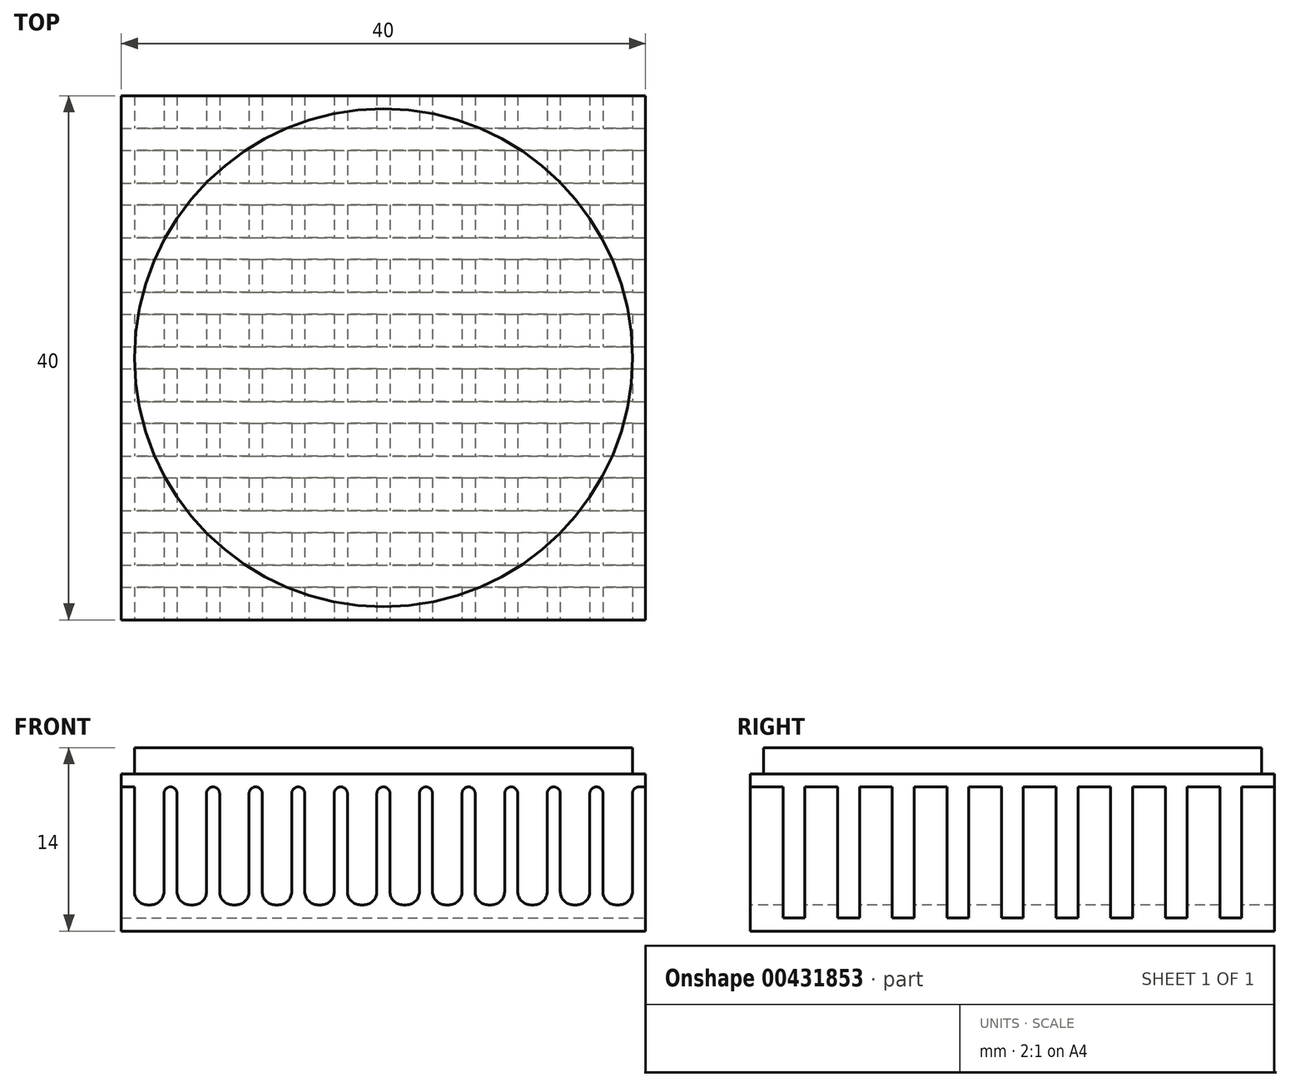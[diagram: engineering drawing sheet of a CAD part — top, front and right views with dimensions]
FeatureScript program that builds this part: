
annotation { "Feature Type Name" : "Feature", "Feature Type Description" : "" }
export const myFeature = defineFeature(function(context is Context, id is Id, definition is map)
    precondition{}
    {
        {
            var Q0;
            Q0=qCreatedBy(makeId("Top.planeOp"),FACE);
            var sketch = newSketch(context, id + "F0", { "sketchPlane" : qUnion([Q0])});
            skLineSegment(sketch, "E0.bottom", {"start": v(20, 20) * mm, "end": v(-20, 20) * mm});
            skLineSegment(sketch, "E0.top", {"start": v(20, -20) * mm, "end": v(-20, -20) * mm});
            skLineSegment(sketch, "E0.left", {"start": v(20, 20) * mm, "end": v(20, -20) * mm});
            skLineSegment(sketch, "E0.right", {"start": v(-20, 20) * mm, "end": v(-20, -20) * mm});
            skPoint(sketch, "E0.middle", {"position": v(0, 0) * mm});
            skSolve(sketch);
        }
        {
            var Q0;
            Q0=makeQuery(id+"F0.imprint","IMPRINT",FACE,{"disambiguationData":[TD([[makeQuery(id+"F0.imprint","IMPRINT",EDGE,{"derivedFrom":sQuery(id+"F0.wireOp",EDGE,"E0.bottom")}),1.0]])]});
            extrude(context, id + "F1", {"entities" : qUnion([Q0]), "depth" : 11 * mm});
        }
        {
            var Q0;
            Q0=makeQuery(id+"F1.opExtrude","SWEPT_FACE",FACE,{"disambiguationData":[OSD([sQuery(id+"F0.wireOp",EDGE,"E0.top")])]});
            var sketch = newSketch(context, id + "F2", { "sketchPlane" : qUnion([Q0])});
            skLineSegment(sketch, "E1.bottom", {"start": v(-19, 11) * mm, "end": v(-16.75, 11) * mm});
            skLineSegment(sketch, "E1.top", {"start": v(-19, 2) * mm, "end": v(-16.75, 2) * mm});
            skLineSegment(sketch, "E1.left", {"start": v(-19, 11) * mm, "end": v(-19, 2) * mm});
            skLineSegment(sketch, "E1.right", {"start": v(-16.75, 11) * mm, "end": v(-16.75, 2) * mm});
            skLineSegment(sketch, "E2.1.0.0", {"start": v(-15.75, 11) * mm, "end": v(-13.5, 11) * mm});
            skLineSegment(sketch, "E2.1.0.1", {"start": v(-13.5, 11) * mm, "end": v(-13.5, 2) * mm});
            skLineSegment(sketch, "E2.1.0.2", {"start": v(-15.75, 2) * mm, "end": v(-13.5, 2) * mm});
            skLineSegment(sketch, "E2.1.0.3", {"start": v(-15.75, 11) * mm, "end": v(-15.75, 2) * mm});
            skLineSegment(sketch, "E2.2.0.0", {"start": v(-12.5, 11) * mm, "end": v(-10.25, 11) * mm});
            skLineSegment(sketch, "E2.2.0.1", {"start": v(-10.25, 11) * mm, "end": v(-10.25, 2) * mm});
            skLineSegment(sketch, "E2.2.0.2", {"start": v(-12.5, 2) * mm, "end": v(-10.25, 2) * mm});
            skLineSegment(sketch, "E2.2.0.3", {"start": v(-12.5, 11) * mm, "end": v(-12.5, 2) * mm});
            skLineSegment(sketch, "E2.3.0.0", {"start": v(-9.25, 11) * mm, "end": v(-7, 11) * mm});
            skLineSegment(sketch, "E2.3.0.1", {"start": v(-7, 11) * mm, "end": v(-7, 2) * mm});
            skLineSegment(sketch, "E2.3.0.2", {"start": v(-9.25, 2) * mm, "end": v(-7, 2) * mm});
            skLineSegment(sketch, "E2.3.0.3", {"start": v(-9.25, 11) * mm, "end": v(-9.25, 2) * mm});
            skLineSegment(sketch, "E2.4.0.0", {"start": v(-6, 11) * mm, "end": v(-3.75, 11) * mm});
            skLineSegment(sketch, "E2.4.0.1", {"start": v(-3.75, 11) * mm, "end": v(-3.75, 2) * mm});
            skLineSegment(sketch, "E2.4.0.2", {"start": v(-6, 2) * mm, "end": v(-3.75, 2) * mm});
            skLineSegment(sketch, "E2.4.0.3", {"start": v(-6, 11) * mm, "end": v(-6, 2) * mm});
            skLineSegment(sketch, "E2.5.0.0", {"start": v(-2.75, 11) * mm, "end": v(-0.5, 11) * mm});
            skLineSegment(sketch, "E2.5.0.1", {"start": v(-0.5, 11) * mm, "end": v(-0.5, 2) * mm});
            skLineSegment(sketch, "E2.5.0.2", {"start": v(-2.75, 2) * mm, "end": v(-0.5, 2) * mm});
            skLineSegment(sketch, "E2.5.0.3", {"start": v(-2.75, 11) * mm, "end": v(-2.75, 2) * mm});
            skLineSegment(sketch, "E2.6.0.0", {"start": v(0.5, 11) * mm, "end": v(2.75, 11) * mm});
            skLineSegment(sketch, "E2.6.0.1", {"start": v(2.75, 11) * mm, "end": v(2.75, 2) * mm});
            skLineSegment(sketch, "E2.6.0.2", {"start": v(0.5, 2) * mm, "end": v(2.75, 2) * mm});
            skLineSegment(sketch, "E2.6.0.3", {"start": v(0.5, 11) * mm, "end": v(0.5, 2) * mm});
            skLineSegment(sketch, "E2.7.0.0", {"start": v(3.75, 11) * mm, "end": v(6, 11) * mm});
            skLineSegment(sketch, "E2.7.0.1", {"start": v(6, 11) * mm, "end": v(6, 2) * mm});
            skLineSegment(sketch, "E2.7.0.2", {"start": v(3.75, 2) * mm, "end": v(6, 2) * mm});
            skLineSegment(sketch, "E2.7.0.3", {"start": v(3.75, 11) * mm, "end": v(3.75, 2) * mm});
            skLineSegment(sketch, "E2.8.0.0", {"start": v(7, 11) * mm, "end": v(9.25, 11) * mm});
            skLineSegment(sketch, "E2.8.0.1", {"start": v(9.25, 11) * mm, "end": v(9.25, 2) * mm});
            skLineSegment(sketch, "E2.8.0.2", {"start": v(7, 2) * mm, "end": v(9.25, 2) * mm});
            skLineSegment(sketch, "E2.8.0.3", {"start": v(7, 11) * mm, "end": v(7, 2) * mm});
            skLineSegment(sketch, "E2.9.0.0", {"start": v(10.25, 11) * mm, "end": v(12.5, 11) * mm});
            skLineSegment(sketch, "E2.9.0.1", {"start": v(12.5, 11) * mm, "end": v(12.5, 2) * mm});
            skLineSegment(sketch, "E2.9.0.2", {"start": v(10.25, 2) * mm, "end": v(12.5, 2) * mm});
            skLineSegment(sketch, "E2.9.0.3", {"start": v(10.25, 11) * mm, "end": v(10.25, 2) * mm});
            skLineSegment(sketch, "E2.10.0.0", {"start": v(13.5, 11) * mm, "end": v(15.75, 11) * mm});
            skLineSegment(sketch, "E2.10.0.1", {"start": v(15.75, 11) * mm, "end": v(15.75, 2) * mm});
            skLineSegment(sketch, "E2.10.0.2", {"start": v(13.5, 2) * mm, "end": v(15.75, 2) * mm});
            skLineSegment(sketch, "E2.10.0.3", {"start": v(13.5, 11) * mm, "end": v(13.5, 2) * mm});
            skLineSegment(sketch, "E2.11.0.0", {"start": v(16.75, 11) * mm, "end": v(19, 11) * mm});
            skLineSegment(sketch, "E2.11.0.1", {"start": v(19, 11) * mm, "end": v(19, 2) * mm});
            skLineSegment(sketch, "E2.11.0.2", {"start": v(16.75, 2) * mm, "end": v(19, 2) * mm});
            skLineSegment(sketch, "E2.11.0.3", {"start": v(16.75, 11) * mm, "end": v(16.75, 2) * mm});
            skLineSegment(sketch, "E2.direction1", {"start": v(-19, 11) * mm, "end": v(-15.75, 11) * mm, "construction": true});
            skSolve(sketch);
        }
        {
            var Q0;
            Q0 = qSketchRegion(id + "F2", true);
            extrude(context, id + "F3", {"entities" : qUnion([Q0]), "operationType" : NewBodyOperationType.REMOVE, "oppositeDirection" : true, "depth" : 40 * mm});
        }
        {
            var Q0;
            Q0=makeQuery(id+"F3.boolean.opBoolean","COPY",EDGE,{"derivedFrom":makeQuery(id+"F3.opExtrude","SWEPT_EDGE",EDGE,{"disambiguationData":[OSD([sQuery(id+"F0.wireOp",EDGE,"E0.top"),sQuery(id+"F2.wireOp",EDGE,"E2.11.0.0"),sQuery(id+"F2.wireOp",EDGE,"E2.11.0.1")])]})});
            var Q1;
            Q1=makeQuery(id+"F3.boolean.opBoolean","COPY",EDGE,{"derivedFrom":makeQuery(id+"F3.opExtrude","SWEPT_EDGE",EDGE,{"disambiguationData":[OSD([sQuery(id+"F0.wireOp",EDGE,"E0.top"),sQuery(id+"F2.wireOp",EDGE,"E2.11.0.0"),sQuery(id+"F2.wireOp",EDGE,"E2.11.0.3")])]})});
            var Q2;
            Q2=makeQuery(id+"F3.boolean.opBoolean","COPY",EDGE,{"derivedFrom":makeQuery(id+"F3.opExtrude","SWEPT_EDGE",EDGE,{"disambiguationData":[OSD([sQuery(id+"F0.wireOp",EDGE,"E0.top"),sQuery(id+"F2.wireOp",EDGE,"E2.10.0.0"),sQuery(id+"F2.wireOp",EDGE,"E2.10.0.1")])]})});
            var Q3;
            Q3=makeQuery(id+"F3.boolean.opBoolean","COPY",EDGE,{"derivedFrom":makeQuery(id+"F3.opExtrude","SWEPT_EDGE",EDGE,{"disambiguationData":[OSD([sQuery(id+"F0.wireOp",EDGE,"E0.top"),sQuery(id+"F2.wireOp",EDGE,"E2.10.0.0"),sQuery(id+"F2.wireOp",EDGE,"E2.10.0.3")])]})});
            var Q4;
            Q4=makeQuery(id+"F3.boolean.opBoolean","COPY",EDGE,{"derivedFrom":makeQuery(id+"F3.opExtrude","SWEPT_EDGE",EDGE,{"disambiguationData":[OSD([sQuery(id+"F0.wireOp",EDGE,"E0.top"),sQuery(id+"F2.wireOp",EDGE,"E2.9.0.0"),sQuery(id+"F2.wireOp",EDGE,"E2.9.0.1")])]})});
            var Q5;
            Q5=makeQuery(id+"F3.boolean.opBoolean","COPY",EDGE,{"derivedFrom":makeQuery(id+"F3.opExtrude","SWEPT_EDGE",EDGE,{"disambiguationData":[OSD([sQuery(id+"F0.wireOp",EDGE,"E0.top"),sQuery(id+"F2.wireOp",EDGE,"E2.9.0.0"),sQuery(id+"F2.wireOp",EDGE,"E2.9.0.3")])]})});
            var Q6;
            Q6=makeQuery(id+"F3.boolean.opBoolean","COPY",EDGE,{"derivedFrom":makeQuery(id+"F3.opExtrude","SWEPT_EDGE",EDGE,{"disambiguationData":[OSD([sQuery(id+"F0.wireOp",EDGE,"E0.top"),sQuery(id+"F2.wireOp",EDGE,"E2.8.0.0"),sQuery(id+"F2.wireOp",EDGE,"E2.8.0.1")])]})});
            var Q7;
            Q7=makeQuery(id+"F3.boolean.opBoolean","COPY",EDGE,{"derivedFrom":makeQuery(id+"F3.opExtrude","SWEPT_EDGE",EDGE,{"disambiguationData":[OSD([sQuery(id+"F0.wireOp",EDGE,"E0.top"),sQuery(id+"F2.wireOp",EDGE,"E2.8.0.0"),sQuery(id+"F2.wireOp",EDGE,"E2.8.0.3")])]})});
            var Q8;
            Q8=makeQuery(id+"F3.boolean.opBoolean","COPY",EDGE,{"derivedFrom":makeQuery(id+"F3.opExtrude","SWEPT_EDGE",EDGE,{"disambiguationData":[OSD([sQuery(id+"F0.wireOp",EDGE,"E0.top"),sQuery(id+"F2.wireOp",EDGE,"E2.7.0.0"),sQuery(id+"F2.wireOp",EDGE,"E2.7.0.1")])]})});
            var Q9;
            Q9=makeQuery(id+"F3.boolean.opBoolean","COPY",EDGE,{"derivedFrom":makeQuery(id+"F3.opExtrude","SWEPT_EDGE",EDGE,{"disambiguationData":[OSD([sQuery(id+"F0.wireOp",EDGE,"E0.top"),sQuery(id+"F2.wireOp",EDGE,"E2.7.0.0"),sQuery(id+"F2.wireOp",EDGE,"E2.7.0.3")])]})});
            var Q10;
            Q10=makeQuery(id+"F3.boolean.opBoolean","COPY",EDGE,{"derivedFrom":makeQuery(id+"F3.opExtrude","SWEPT_EDGE",EDGE,{"disambiguationData":[OSD([sQuery(id+"F0.wireOp",EDGE,"E0.top"),sQuery(id+"F2.wireOp",EDGE,"E2.6.0.0"),sQuery(id+"F2.wireOp",EDGE,"E2.6.0.3")])]})});
            var Q11;
            Q11=makeQuery(id+"F3.boolean.opBoolean","COPY",EDGE,{"derivedFrom":makeQuery(id+"F3.opExtrude","SWEPT_EDGE",EDGE,{"disambiguationData":[OSD([sQuery(id+"F0.wireOp",EDGE,"E0.top"),sQuery(id+"F2.wireOp",EDGE,"E2.5.0.0"),sQuery(id+"F2.wireOp",EDGE,"E2.5.0.1")])]})});
            var Q12;
            Q12=makeQuery(id+"F3.boolean.opBoolean","COPY",EDGE,{"derivedFrom":makeQuery(id+"F3.opExtrude","SWEPT_EDGE",EDGE,{"disambiguationData":[OSD([sQuery(id+"F0.wireOp",EDGE,"E0.top"),sQuery(id+"F2.wireOp",EDGE,"E2.5.0.0"),sQuery(id+"F2.wireOp",EDGE,"E2.5.0.3")])]})});
            var Q13;
            Q13=makeQuery(id+"F3.boolean.opBoolean","COPY",EDGE,{"derivedFrom":makeQuery(id+"F3.opExtrude","SWEPT_EDGE",EDGE,{"disambiguationData":[OSD([sQuery(id+"F0.wireOp",EDGE,"E0.top"),sQuery(id+"F2.wireOp",EDGE,"E2.4.0.0"),sQuery(id+"F2.wireOp",EDGE,"E2.4.0.1")])]})});
            var Q14;
            Q14=makeQuery(id+"F3.boolean.opBoolean","COPY",EDGE,{"derivedFrom":makeQuery(id+"F3.opExtrude","SWEPT_EDGE",EDGE,{"disambiguationData":[OSD([sQuery(id+"F0.wireOp",EDGE,"E0.top"),sQuery(id+"F2.wireOp",EDGE,"E2.4.0.0"),sQuery(id+"F2.wireOp",EDGE,"E2.4.0.3")])]})});
            var Q15;
            Q15=makeQuery(id+"F3.boolean.opBoolean","COPY",EDGE,{"derivedFrom":makeQuery(id+"F3.opExtrude","SWEPT_EDGE",EDGE,{"disambiguationData":[OSD([sQuery(id+"F0.wireOp",EDGE,"E0.top"),sQuery(id+"F2.wireOp",EDGE,"E2.3.0.0"),sQuery(id+"F2.wireOp",EDGE,"E2.3.0.1")])]})});
            var Q16;
            Q16=makeQuery(id+"F3.boolean.opBoolean","COPY",EDGE,{"derivedFrom":makeQuery(id+"F3.opExtrude","SWEPT_EDGE",EDGE,{"disambiguationData":[OSD([sQuery(id+"F0.wireOp",EDGE,"E0.top"),sQuery(id+"F2.wireOp",EDGE,"E2.3.0.0"),sQuery(id+"F2.wireOp",EDGE,"E2.3.0.3")])]})});
            var Q17;
            Q17=makeQuery(id+"F3.boolean.opBoolean","COPY",EDGE,{"derivedFrom":makeQuery(id+"F3.opExtrude","SWEPT_EDGE",EDGE,{"disambiguationData":[OSD([sQuery(id+"F0.wireOp",EDGE,"E0.top"),sQuery(id+"F2.wireOp",EDGE,"E2.2.0.0"),sQuery(id+"F2.wireOp",EDGE,"E2.2.0.1")])]})});
            var Q18;
            Q18=makeQuery(id+"F3.boolean.opBoolean","COPY",EDGE,{"derivedFrom":makeQuery(id+"F3.opExtrude","SWEPT_EDGE",EDGE,{"disambiguationData":[OSD([sQuery(id+"F0.wireOp",EDGE,"E0.top"),sQuery(id+"F2.wireOp",EDGE,"E2.2.0.0"),sQuery(id+"F2.wireOp",EDGE,"E2.2.0.3")])]})});
            var Q19;
            Q19=makeQuery(id+"F3.boolean.opBoolean","COPY",EDGE,{"derivedFrom":makeQuery(id+"F3.opExtrude","SWEPT_EDGE",EDGE,{"disambiguationData":[OSD([sQuery(id+"F0.wireOp",EDGE,"E0.top"),sQuery(id+"F2.wireOp",EDGE,"E2.1.0.0"),sQuery(id+"F2.wireOp",EDGE,"E2.1.0.1")])]})});
            var Q20;
            Q20=makeQuery(id+"F3.boolean.opBoolean","COPY",EDGE,{"derivedFrom":makeQuery(id+"F3.opExtrude","SWEPT_EDGE",EDGE,{"disambiguationData":[OSD([sQuery(id+"F0.wireOp",EDGE,"E0.top"),sQuery(id+"F2.wireOp",EDGE,"E2.1.0.0"),sQuery(id+"F2.wireOp",EDGE,"E2.1.0.3")])]})});
            var Q21;
            Q21=makeQuery(id+"F3.boolean.opBoolean","COPY",EDGE,{"derivedFrom":makeQuery(id+"F3.opExtrude","SWEPT_EDGE",EDGE,{"disambiguationData":[OSD([sQuery(id+"F0.wireOp",EDGE,"E0.top"),sQuery(id+"F2.wireOp",EDGE,"E1.bottom"),sQuery(id+"F2.wireOp",EDGE,"E1.right")])]})});
            var Q22;
            Q22=makeQuery(id+"F3.boolean.opBoolean","COPY",EDGE,{"derivedFrom":makeQuery(id+"F3.opExtrude","SWEPT_EDGE",EDGE,{"disambiguationData":[OSD([sQuery(id+"F0.wireOp",EDGE,"E0.top"),sQuery(id+"F2.wireOp",EDGE,"E1.bottom"),sQuery(id+"F2.wireOp",EDGE,"E1.left")])]})});
            var Q23;
            Q23=makeQuery(id+"F3.boolean.opBoolean","COPY",EDGE,{"derivedFrom":makeQuery(id+"F3.opExtrude","SWEPT_EDGE",EDGE,{"disambiguationData":[OSD([sQuery(id+"F0.wireOp",EDGE,"E0.top"),sQuery(id+"F2.wireOp",EDGE,"E2.6.0.0"),sQuery(id+"F2.wireOp",EDGE,"E2.6.0.1")])]})});
            fillet(context, id + "F4", {"entities" : qUnion([Q0, Q1, Q2, Q3, Q4, Q5, Q6, Q7, Q8, Q9, Q10, Q11, Q12, Q13, Q14, Q15, Q16, Q17, Q18, Q19, Q20, Q21, Q22, Q23]), "radius" : 0.5 * mm, "tangentPropagation" : true, "allowEdgeOverflow" : false});
        }
        {
            var Q0;
            Q0=makeQuery(id+"F3.boolean.opBoolean","COPY",EDGE,{"derivedFrom":makeQuery(id+"F3.opExtrude","SWEPT_EDGE",EDGE,{"disambiguationData":[OSD([sQuery(id+"F2.wireOp",EDGE,"E1.top"),sQuery(id+"F2.wireOp",EDGE,"E1.left")])]})});
            var Q1;
            Q1=makeQuery(id+"F3.boolean.opBoolean","COPY",EDGE,{"derivedFrom":makeQuery(id+"F3.opExtrude","SWEPT_EDGE",EDGE,{"disambiguationData":[OSD([sQuery(id+"F2.wireOp",EDGE,"E2.1.0.2"),sQuery(id+"F2.wireOp",EDGE,"E2.1.0.3")])]})});
            var Q2;
            Q2=makeQuery(id+"F3.boolean.opBoolean","COPY",EDGE,{"derivedFrom":makeQuery(id+"F3.opExtrude","SWEPT_EDGE",EDGE,{"disambiguationData":[OSD([sQuery(id+"F2.wireOp",EDGE,"E2.2.0.2"),sQuery(id+"F2.wireOp",EDGE,"E2.2.0.3")])]})});
            var Q3;
            Q3=makeQuery(id+"F3.boolean.opBoolean","COPY",EDGE,{"derivedFrom":makeQuery(id+"F3.opExtrude","SWEPT_EDGE",EDGE,{"disambiguationData":[OSD([sQuery(id+"F2.wireOp",EDGE,"E2.3.0.2"),sQuery(id+"F2.wireOp",EDGE,"E2.3.0.3")])]})});
            var Q4;
            Q4=makeQuery(id+"F3.boolean.opBoolean","COPY",EDGE,{"derivedFrom":makeQuery(id+"F3.opExtrude","SWEPT_EDGE",EDGE,{"disambiguationData":[OSD([sQuery(id+"F2.wireOp",EDGE,"E2.4.0.2"),sQuery(id+"F2.wireOp",EDGE,"E2.4.0.3")])]})});
            var Q5;
            Q5=makeQuery(id+"F3.boolean.opBoolean","COPY",EDGE,{"derivedFrom":makeQuery(id+"F3.opExtrude","SWEPT_EDGE",EDGE,{"disambiguationData":[OSD([sQuery(id+"F2.wireOp",EDGE,"E2.5.0.2"),sQuery(id+"F2.wireOp",EDGE,"E2.5.0.3")])]})});
            var Q6;
            Q6=makeQuery(id+"F3.boolean.opBoolean","COPY",EDGE,{"derivedFrom":makeQuery(id+"F3.opExtrude","SWEPT_EDGE",EDGE,{"disambiguationData":[OSD([sQuery(id+"F2.wireOp",EDGE,"E2.6.0.2"),sQuery(id+"F2.wireOp",EDGE,"E2.6.0.3")])]})});
            var Q7;
            Q7=makeQuery(id+"F3.boolean.opBoolean","COPY",EDGE,{"derivedFrom":makeQuery(id+"F3.opExtrude","SWEPT_EDGE",EDGE,{"disambiguationData":[OSD([sQuery(id+"F2.wireOp",EDGE,"E2.7.0.2"),sQuery(id+"F2.wireOp",EDGE,"E2.7.0.3")])]})});
            var Q8;
            Q8=makeQuery(id+"F3.boolean.opBoolean","COPY",EDGE,{"derivedFrom":makeQuery(id+"F3.opExtrude","SWEPT_EDGE",EDGE,{"disambiguationData":[OSD([sQuery(id+"F2.wireOp",EDGE,"E2.8.0.2"),sQuery(id+"F2.wireOp",EDGE,"E2.8.0.3")])]})});
            var Q9;
            Q9=makeQuery(id+"F3.boolean.opBoolean","COPY",EDGE,{"derivedFrom":makeQuery(id+"F3.opExtrude","SWEPT_EDGE",EDGE,{"disambiguationData":[OSD([sQuery(id+"F2.wireOp",EDGE,"E2.9.0.2"),sQuery(id+"F2.wireOp",EDGE,"E2.9.0.3")])]})});
            var Q10;
            Q10=makeQuery(id+"F3.boolean.opBoolean","COPY",EDGE,{"derivedFrom":makeQuery(id+"F3.opExtrude","SWEPT_EDGE",EDGE,{"disambiguationData":[OSD([sQuery(id+"F2.wireOp",EDGE,"E2.10.0.2"),sQuery(id+"F2.wireOp",EDGE,"E2.10.0.3")])]})});
            var Q11;
            Q11=makeQuery(id+"F3.boolean.opBoolean","COPY",EDGE,{"derivedFrom":makeQuery(id+"F3.opExtrude","SWEPT_EDGE",EDGE,{"disambiguationData":[OSD([sQuery(id+"F2.wireOp",EDGE,"E2.11.0.2"),sQuery(id+"F2.wireOp",EDGE,"E2.11.0.3")])]})});
            var Q12;
            Q12=makeQuery(id+"F3.boolean.opBoolean","COPY",EDGE,{"derivedFrom":makeQuery(id+"F3.opExtrude","SWEPT_EDGE",EDGE,{"disambiguationData":[OSD([sQuery(id+"F2.wireOp",EDGE,"E1.top"),sQuery(id+"F2.wireOp",EDGE,"E1.right")])]})});
            var Q13;
            Q13=makeQuery(id+"F3.boolean.opBoolean","COPY",EDGE,{"derivedFrom":makeQuery(id+"F3.opExtrude","SWEPT_EDGE",EDGE,{"disambiguationData":[OSD([sQuery(id+"F2.wireOp",EDGE,"E2.1.0.1"),sQuery(id+"F2.wireOp",EDGE,"E2.1.0.2")])]})});
            var Q14;
            Q14=makeQuery(id+"F3.boolean.opBoolean","COPY",EDGE,{"derivedFrom":makeQuery(id+"F3.opExtrude","SWEPT_EDGE",EDGE,{"disambiguationData":[OSD([sQuery(id+"F2.wireOp",EDGE,"E2.2.0.1"),sQuery(id+"F2.wireOp",EDGE,"E2.2.0.2")])]})});
            var Q15;
            Q15=makeQuery(id+"F3.boolean.opBoolean","COPY",EDGE,{"derivedFrom":makeQuery(id+"F3.opExtrude","SWEPT_EDGE",EDGE,{"disambiguationData":[OSD([sQuery(id+"F2.wireOp",EDGE,"E2.3.0.1"),sQuery(id+"F2.wireOp",EDGE,"E2.3.0.2")])]})});
            var Q16;
            Q16=makeQuery(id+"F3.boolean.opBoolean","COPY",EDGE,{"derivedFrom":makeQuery(id+"F3.opExtrude","SWEPT_EDGE",EDGE,{"disambiguationData":[OSD([sQuery(id+"F2.wireOp",EDGE,"E2.4.0.1"),sQuery(id+"F2.wireOp",EDGE,"E2.4.0.2")])]})});
            var Q17;
            Q17=makeQuery(id+"F3.boolean.opBoolean","COPY",EDGE,{"derivedFrom":makeQuery(id+"F3.opExtrude","SWEPT_EDGE",EDGE,{"disambiguationData":[OSD([sQuery(id+"F2.wireOp",EDGE,"E2.5.0.1"),sQuery(id+"F2.wireOp",EDGE,"E2.5.0.2")])]})});
            var Q18;
            Q18=makeQuery(id+"F3.boolean.opBoolean","COPY",EDGE,{"derivedFrom":makeQuery(id+"F3.opExtrude","SWEPT_EDGE",EDGE,{"disambiguationData":[OSD([sQuery(id+"F2.wireOp",EDGE,"E2.6.0.1"),sQuery(id+"F2.wireOp",EDGE,"E2.6.0.2")])]})});
            var Q19;
            Q19=makeQuery(id+"F3.boolean.opBoolean","COPY",EDGE,{"derivedFrom":makeQuery(id+"F3.opExtrude","SWEPT_EDGE",EDGE,{"disambiguationData":[OSD([sQuery(id+"F2.wireOp",EDGE,"E2.7.0.1"),sQuery(id+"F2.wireOp",EDGE,"E2.7.0.2")])]})});
            var Q20;
            Q20=makeQuery(id+"F3.boolean.opBoolean","COPY",EDGE,{"derivedFrom":makeQuery(id+"F3.opExtrude","SWEPT_EDGE",EDGE,{"disambiguationData":[OSD([sQuery(id+"F2.wireOp",EDGE,"E2.8.0.1"),sQuery(id+"F2.wireOp",EDGE,"E2.8.0.2")])]})});
            var Q21;
            Q21=makeQuery(id+"F3.boolean.opBoolean","COPY",EDGE,{"derivedFrom":makeQuery(id+"F3.opExtrude","SWEPT_EDGE",EDGE,{"disambiguationData":[OSD([sQuery(id+"F2.wireOp",EDGE,"E2.9.0.1"),sQuery(id+"F2.wireOp",EDGE,"E2.9.0.2")])]})});
            var Q22;
            Q22=makeQuery(id+"F3.boolean.opBoolean","COPY",EDGE,{"derivedFrom":makeQuery(id+"F3.opExtrude","SWEPT_EDGE",EDGE,{"disambiguationData":[OSD([sQuery(id+"F2.wireOp",EDGE,"E2.10.0.1"),sQuery(id+"F2.wireOp",EDGE,"E2.10.0.2")])]})});
            var Q23;
            Q23=makeQuery(id+"F3.boolean.opBoolean","COPY",EDGE,{"derivedFrom":makeQuery(id+"F3.opExtrude","SWEPT_EDGE",EDGE,{"disambiguationData":[OSD([sQuery(id+"F2.wireOp",EDGE,"E2.11.0.1"),sQuery(id+"F2.wireOp",EDGE,"E2.11.0.2")])]})});
            fillet(context, id + "F5", {"entities" : qUnion([Q0, Q1, Q2, Q3, Q4, Q5, Q6, Q7, Q8, Q9, Q10, Q11, Q12, Q13, Q14, Q15, Q16, Q17, Q18, Q19, Q20, Q21, Q22, Q23]), "radius" : 1 * mm, "tangentPropagation" : true, "allowEdgeOverflow" : false});
        }
        {
            var Q0;
            Q0=makeQuery(id+"F1.opExtrude","SWEPT_FACE",FACE,{"disambiguationData":[OSD([sQuery(id+"F0.wireOp",EDGE,"E0.left")])]});
            var sketch = newSketch(context, id + "F6", { "sketchPlane" : qUnion([Q0])});
            skLineSegment(sketch, "E3.bottom", {"start": v(-17.5, 1) * mm, "end": v(-15.83, 1) * mm});
            skLineSegment(sketch, "E3.top", {"start": v(-17.5, 11) * mm, "end": v(-15.83, 11) * mm});
            skLineSegment(sketch, "E3.left", {"start": v(-17.5, 1) * mm, "end": v(-17.5, 11) * mm});
            skLineSegment(sketch, "E3.right", {"start": v(-15.83, 1) * mm, "end": v(-15.83, 11) * mm});
            skLineSegment(sketch, "E4.1.0.0", {"start": v(-11.67, 1) * mm, "end": v(-11.67, 11) * mm});
            skLineSegment(sketch, "E4.1.0.1", {"start": v(-13.33, 11) * mm, "end": v(-11.67, 11) * mm});
            skLineSegment(sketch, "E4.1.0.2", {"start": v(-13.33, 1) * mm, "end": v(-13.33, 11) * mm});
            skLineSegment(sketch, "E4.1.0.3", {"start": v(-13.33, 1) * mm, "end": v(-11.67, 1) * mm});
            skLineSegment(sketch, "E4.2.0.0", {"start": v(-7.5, 1) * mm, "end": v(-7.5, 11) * mm});
            skLineSegment(sketch, "E4.2.0.1", {"start": v(-9.17, 11) * mm, "end": v(-7.5, 11) * mm});
            skLineSegment(sketch, "E4.2.0.2", {"start": v(-9.17, 1) * mm, "end": v(-9.17, 11) * mm});
            skLineSegment(sketch, "E4.2.0.3", {"start": v(-9.17, 1) * mm, "end": v(-7.5, 1) * mm});
            skLineSegment(sketch, "E4.3.0.0", {"start": v(-3.33, 1) * mm, "end": v(-3.33, 11) * mm});
            skLineSegment(sketch, "E4.3.0.1", {"start": v(-5, 11) * mm, "end": v(-3.33, 11) * mm});
            skLineSegment(sketch, "E4.3.0.2", {"start": v(-5, 1) * mm, "end": v(-5, 11) * mm});
            skLineSegment(sketch, "E4.3.0.3", {"start": v(-5, 1) * mm, "end": v(-3.33, 1) * mm});
            skLineSegment(sketch, "E4.4.0.0", {"start": v(0.83, 1) * mm, "end": v(0.83, 11) * mm});
            skLineSegment(sketch, "E4.4.0.1", {"start": v(-0.83, 11) * mm, "end": v(0.83, 11) * mm});
            skLineSegment(sketch, "E4.4.0.2", {"start": v(-0.83, 1) * mm, "end": v(-0.83, 11) * mm});
            skLineSegment(sketch, "E4.4.0.3", {"start": v(-0.83, 1) * mm, "end": v(0.83, 1) * mm});
            skLineSegment(sketch, "E4.5.0.0", {"start": v(5, 1) * mm, "end": v(5, 11) * mm});
            skLineSegment(sketch, "E4.5.0.1", {"start": v(3.33, 11) * mm, "end": v(5, 11) * mm});
            skLineSegment(sketch, "E4.5.0.2", {"start": v(3.33, 1) * mm, "end": v(3.33, 11) * mm});
            skLineSegment(sketch, "E4.5.0.3", {"start": v(3.33, 1) * mm, "end": v(5, 1) * mm});
            skLineSegment(sketch, "E4.6.0.0", {"start": v(9.17, 1) * mm, "end": v(9.17, 11) * mm});
            skLineSegment(sketch, "E4.6.0.1", {"start": v(7.5, 11) * mm, "end": v(9.17, 11) * mm});
            skLineSegment(sketch, "E4.6.0.2", {"start": v(7.5, 1) * mm, "end": v(7.5, 11) * mm});
            skLineSegment(sketch, "E4.6.0.3", {"start": v(7.5, 1) * mm, "end": v(9.17, 1) * mm});
            skLineSegment(sketch, "E4.7.0.0", {"start": v(13.33, 1) * mm, "end": v(13.33, 11) * mm});
            skLineSegment(sketch, "E4.7.0.1", {"start": v(11.67, 11) * mm, "end": v(13.33, 11) * mm});
            skLineSegment(sketch, "E4.7.0.2", {"start": v(11.67, 1) * mm, "end": v(11.67, 11) * mm});
            skLineSegment(sketch, "E4.7.0.3", {"start": v(11.67, 1) * mm, "end": v(13.33, 1) * mm});
            skLineSegment(sketch, "E4.8.0.0", {"start": v(17.5, 1) * mm, "end": v(17.5, 11) * mm});
            skLineSegment(sketch, "E4.8.0.1", {"start": v(15.83, 11) * mm, "end": v(17.5, 11) * mm});
            skLineSegment(sketch, "E4.8.0.2", {"start": v(15.83, 1) * mm, "end": v(15.83, 11) * mm});
            skLineSegment(sketch, "E4.8.0.3", {"start": v(15.83, 1) * mm, "end": v(17.5, 1) * mm});
            skLineSegment(sketch, "E4.direction1", {"start": v(-15.83, 1) * mm, "end": v(-11.67, 1) * mm, "construction": true});
            skSolve(sketch);
        }
        {
            var Q0;
            Q0 = qSketchRegion(id + "F6", true);
            extrude(context, id + "F7", {"entities" : qUnion([Q0]), "operationType" : NewBodyOperationType.REMOVE, "oppositeDirection" : true, "depth" : 40 * mm});
        }
        {
            var Q0;
            Q0=qCreatedBy(makeId("Top.planeOp"),FACE);
            cPlane(context, id + "F8", {"entities" : qUnion([Q0]), "cplaneType" : CPlaneType.OFFSET, "offset" : 12 * mm, "width" : 150 * mm, "height" : 150 * mm});
        }
        {
            var Q0;
            Q0=qCreatedBy(id+"F8.planeOp",FACE);
            var sketch = newSketch(context, id + "F9", { "sketchPlane" : qUnion([Q0])});
            skLineSegment(sketch, "E5.bottom", {"start": v(-20, 20) * mm, "end": v(20, 20) * mm});
            skLineSegment(sketch, "E5.top", {"start": v(-20, -20) * mm, "end": v(20, -20) * mm});
            skLineSegment(sketch, "E5.left", {"start": v(-20, 20) * mm, "end": v(-20, -20) * mm});
            skLineSegment(sketch, "E5.right", {"start": v(20, 20) * mm, "end": v(20, -20) * mm});
            skPoint(sketch, "E5.middle", {"position": v(0, 0) * mm});
            skSolve(sketch);
        }
        {
            var Q0;
            Q0=makeQuery(id+"F9.imprint","IMPRINT",FACE,{"disambiguationData":[TD([[makeQuery(id+"F9.imprint","IMPRINT",EDGE,{"derivedFrom":sQuery(id+"F9.wireOp",EDGE,"E5.bottom")}),-1.0]])]});
            var Q1;
            {var subQ0=sQuery(id+"F2.wireOp",EDGE,"E1.top");var subQ1=sQuery(id+"F2.wireOp",EDGE,"E1.left");Q1=makeQuery(id+"F7.boolean.opBoolean","SPLIT",FACE,{"disambiguationData":[TD([makeQuery(id+"F1.opExtrude","SWEPT_FACE",FACE,{"disambiguationData":[OSD([sQuery(id+"F0.wireOp",EDGE,"E0.top")])]})])],"derivedFrom":makeQuery(id+"F5.opFillet","BLEND_FACE",FACE,{"disambiguationData":[OSD([subQ0,subQ1])]})});}
            var Q2;
            Q2=makeQuery(id+"F1.opExtrude","SWEPT_BODY",BODY,{"disambiguationData":[OSD([sQuery(id+"F0.wireOp",EDGE,"E0.bottom"),sQuery(id+"F0.wireOp",EDGE,"E0.top"),sQuery(id+"F0.wireOp",EDGE,"E0.left"),sQuery(id+"F0.wireOp",EDGE,"E0.right")])]});
            extrude(context, id + "F10", {"entities" : qUnion([Q0]), "endBound" : BoundingType.UP_TO_BODY, "oppositeDirection" : true, "endBoundEntityFace" : qUnion([Q1]), "endBoundEntityBody" : qUnion([Q2]), "depth" : 25 * mm});
        }
        {
            var Q0;
            Q0=qCreatedBy(id+"F8.planeOp",FACE);
            var sketch = newSketch(context, id + "F11", { "sketchPlane" : qUnion([Q0])});
            skCircle(sketch, "E6", {"center": v(0, 0) * mm, "radius": 19 * mm});
            skPoint(sketch, "E7.0.end.orphan", {"position": v(20, -20) * mm});
            skPoint(sketch, "E8.0.end.orphan", {"position": v(-20, -20) * mm});
            skPoint(sketch, "E9.orphan", {"position": v(-20, 20) * mm});
            skPoint(sketch, "E10.0.end.orphan", {"position": v(20, 20) * mm});
            skPoint(sketch, "E11.trimOffspring.end.orphan", {"position": v(0, 20) * mm});
            skPoint(sketch, "E12.start.orphan", {"position": v(0, -20) * mm});
            skSolve(sketch);
        }
        {
            var Q0;
            Q0 = qSketchRegion(id + "F11", true);
            extrude(context, id + "F12", {"entities" : qUnion([Q0]), "operationType" : NewBodyOperationType.ADD, "depth" : 2 * mm});
        }
    });
